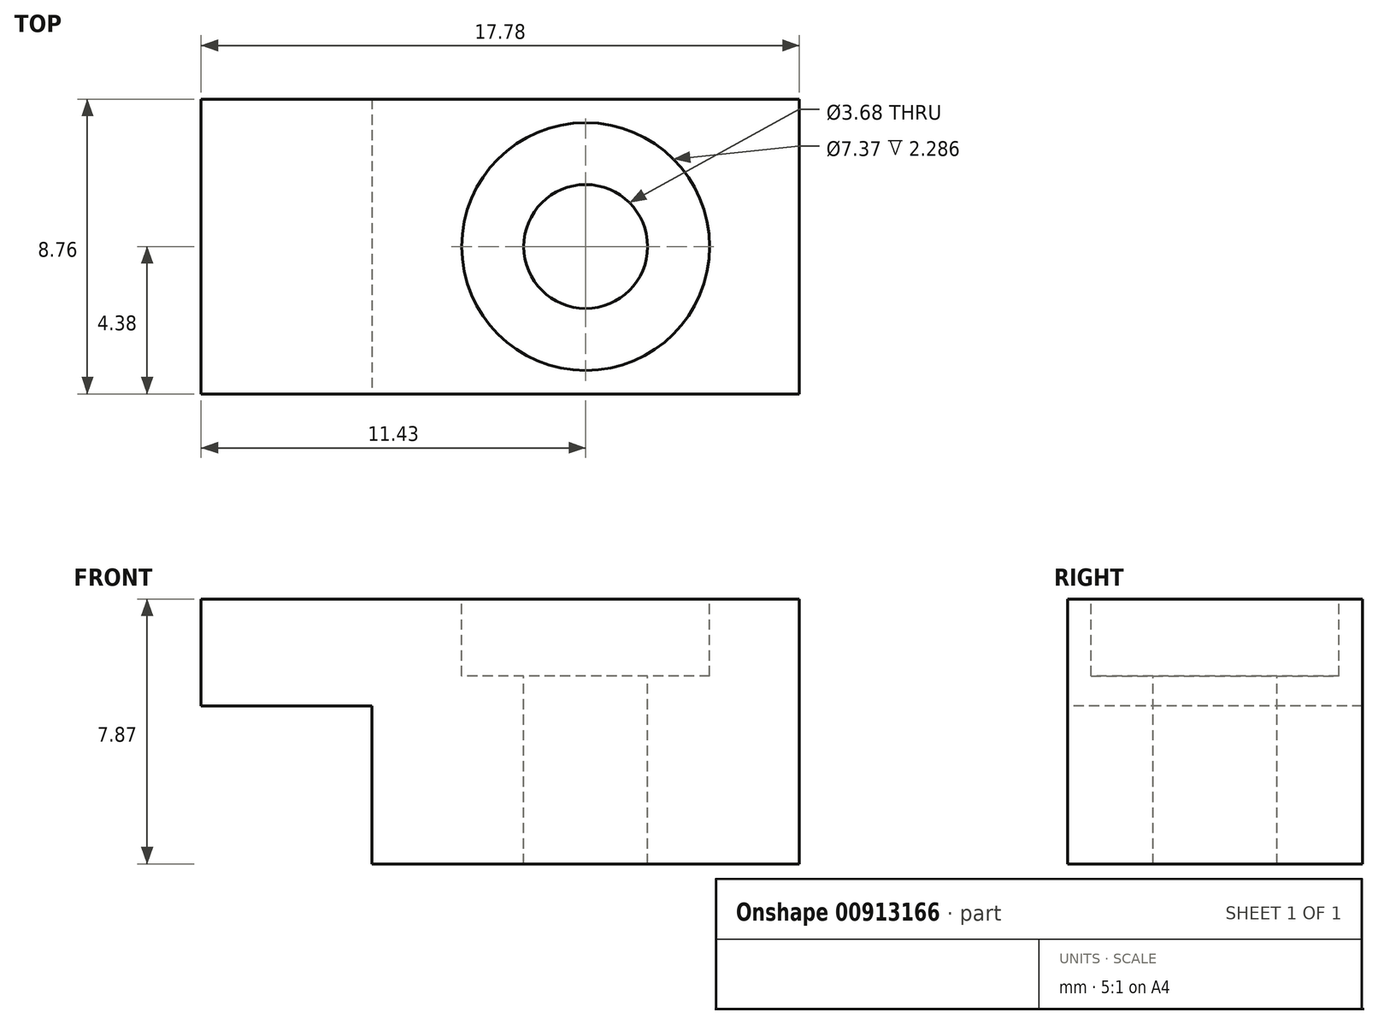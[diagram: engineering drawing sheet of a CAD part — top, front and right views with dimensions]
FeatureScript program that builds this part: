
annotation { "Feature Type Name" : "Feature", "Feature Type Description" : "" }
export const myFeature = defineFeature(function(context is Context, id is Id, definition is map)
    precondition{}
    {
        {
            var Q0;
            Q0=qCreatedBy(makeId("Top.planeOp"),FACE);
            var sketch = newSketch(context, id + "F0", { "sketchPlane" : qUnion([Q0])});
            skLineSegment(sketch, "E0.bottom", {"start": v(6.35, 4.38) * mm, "end": v(-6.35, 4.38) * mm});
            skLineSegment(sketch, "E0.top", {"start": v(6.35, -4.38) * mm, "end": v(-6.35, -4.38) * mm});
            skLineSegment(sketch, "E0.left", {"start": v(6.35, 4.38) * mm, "end": v(6.35, -4.38) * mm});
            skLineSegment(sketch, "E0.right", {"start": v(-6.35, 4.38) * mm, "end": v(-6.35, -4.38) * mm});
            skPoint(sketch, "E0.middle", {"position": v(0, 0) * mm});
            skSolve(sketch);
        }
        {
            var Q0;
            Q0=makeQuery(id+"F0.imprint","IMPRINT",FACE,{"disambiguationData":[TD([[makeQuery(id+"F0.imprint","IMPRINT",EDGE,{"derivedFrom":sQuery(id+"F0.wireOp",EDGE,"E0.bottom")}),1.0]])]});
            extrude(context, id + "F1", {"entities" : qUnion([Q0]), "depth" : 3.17 * mm, "offsetDistance" : 25.4 * mm});
        }
        {
            var Q0;
            Q0=makeQuery(id+"F1.opExtrude","SWEPT_FACE",FACE,{"disambiguationData":[OSD([sQuery(id+"F0.wireOp",EDGE,"E0.top")])]});
            var sketch = newSketch(context, id + "F2", { "sketchPlane" : qUnion([Q0])});
            skLineSegment(sketch, "E1.bottom", {"start": v(6.35, 3.18) * mm, "end": v(-11.43, 3.18) * mm});
            skLineSegment(sketch, "E1.top", {"start": v(6.35, 6.35) * mm, "end": v(-11.43, 6.35) * mm});
            skLineSegment(sketch, "E1.left", {"start": v(6.35, 3.18) * mm, "end": v(6.35, 6.35) * mm});
            skLineSegment(sketch, "E1.right", {"start": v(-11.43, 3.17) * mm, "end": v(-11.43, 6.35) * mm});
            skSolve(sketch);
        }
        {
            var Q0;
            Q0=makeQuery(id+"F2.imprint","IMPRINT",FACE,{"disambiguationData":[TD([[makeQuery(id+"F2.imprint","IMPRINT",EDGE,{"derivedFrom":sQuery(id+"F2.wireOp",EDGE,"E1.top")}),1.0]])]});
            extrude(context, id + "F3", {"entities" : qUnion([Q0]), "operationType" : NewBodyOperationType.ADD, "oppositeDirection" : true, "depth" : 8.76 * mm, "offsetDistance" : 25.4 * mm});
        }
        {
            var Q0;
            Q0=makeQuery(id+"F3.opExtrude","SWEPT_FACE",FACE,{"disambiguationData":[OSD([sQuery(id+"F2.wireOp",EDGE,"E1.top")])]});
            var sketch = newSketch(context, id + "F4", { "sketchPlane" : qUnion([Q0])});
            skCircle(sketch, "E2", {"center": v(0, 0) * mm, "radius": 1.84 * mm});
            skSolve(sketch);
        }
        {
            var Q0;
            Q0=makeQuery(id+"F4.imprint","IMPRINT",FACE,{"disambiguationData":[TD([[makeQuery(id+"F4.imprint","IMPRINT",EDGE,{"derivedFrom":sQuery(id+"F4.wireOp",EDGE,"E2")}),1.0]])]});
            extrude(context, id + "F5", {"entities" : qUnion([Q0]), "operationType" : NewBodyOperationType.REMOVE, "oppositeDirection" : true, "depth" : 25.4 * mm, "offsetDistance" : 25.4 * mm});
        }
        {
            var Q0;
            Q0=makeQuery(id+"F3.opExtrude","SWEPT_FACE",FACE,{"disambiguationData":[OSD([sQuery(id+"F2.wireOp",EDGE,"E1.top")])]});
            var sketch = newSketch(context, id + "F6", { "sketchPlane" : qUnion([Q0])});
            skCircle(sketch, "E3", {"center": v(0, 0) * mm, "radius": 3.68 * mm});
            skSolve(sketch);
        }
        {
            var Q0;
            Q0=makeQuery(id+"F6.imprint","IMPRINT",FACE,{"disambiguationData":[TD([[makeQuery(id+"F6.imprint","IMPRINT",EDGE,{"derivedFrom":sQuery(id+"F6.wireOp",EDGE,"E3")}),1.0]])]});
            extrude(context, id + "F7", {"entities" : qUnion([Q0]), "operationType" : NewBodyOperationType.REMOVE, "oppositeDirection" : true, "depth" : 2.3 * mm, "offsetDistance" : 25.4 * mm});
        }
        {
            var Q0;
            Q0=makeQuery(id+"F1.opExtrude","CAP_FACE",FACE,{"disambiguationData":[OSD([sQuery(id+"F0.wireOp",EDGE,"E0.bottom"),sQuery(id+"F0.wireOp",EDGE,"E0.top"),sQuery(id+"F0.wireOp",EDGE,"E0.left"),sQuery(id+"F0.wireOp",EDGE,"E0.right")])],"isStart":true});
            var sketch = newSketch(context, id + "F8", { "sketchPlane" : qUnion([Q0])});
            skLineSegment(sketch, "E4.bottom", {"start": v(-6.35, -4.38) * mm, "end": v(6.35, -4.38) * mm});
            skLineSegment(sketch, "E4.top", {"start": v(-6.35, 4.38) * mm, "end": v(6.35, 4.38) * mm});
            skLineSegment(sketch, "E4.left", {"start": v(-6.35, -4.38) * mm, "end": v(-6.35, 4.38) * mm});
            skLineSegment(sketch, "E4.right", {"start": v(6.35, -4.38) * mm, "end": v(6.35, 4.38) * mm});
            skCircle(sketch, "E5", {"center": v(0, 0) * mm, "radius": 1.84 * mm});
            skSolve(sketch);
        }
        {
            var Q0;
            Q0 = qSketchRegion(id + "F8", true);
            extrude(context, id + "F9", {"entities" : qUnion([Q0]), "operationType" : NewBodyOperationType.ADD, "depth" : 1.52 * mm, "offsetDistance" : 25.4 * mm});
        }
    });
